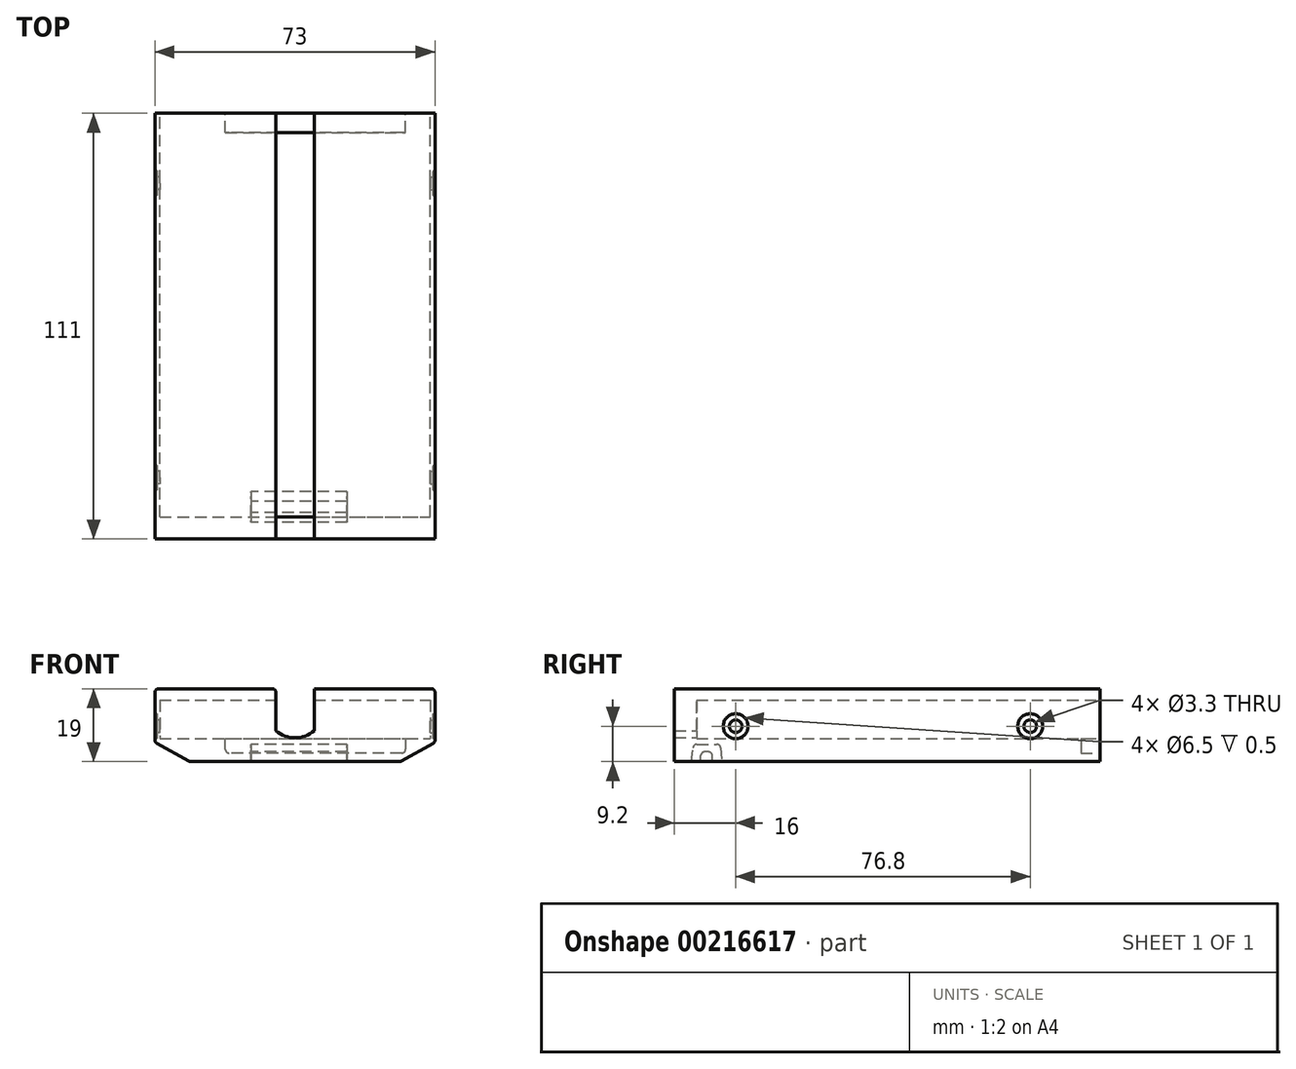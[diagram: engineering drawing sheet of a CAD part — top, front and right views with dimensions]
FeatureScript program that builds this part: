
annotation { "Feature Type Name" : "Feature", "Feature Type Description" : "" }
export const myFeature = defineFeature(function(context is Context, id is Id, definition is map)
    precondition{}
    {
        {
            var Q0;
            Q0=qCreatedBy(makeId("Front.planeOp"),FACE);
            var sketch = newSketch(context, id + "F0", { "sketchPlane" : qUnion([Q0])});
            skLineSegment(sketch, "E0", {"start": v(0, 19) * mm, "end": v(73, 19) * mm});
            skLineSegment(sketch, "E1", {"start": v(73, 19) * mm, "end": v(73, 5) * mm});
            skLineSegment(sketch, "E2", {"start": v(73, 5) * mm, "end": v(64, 0) * mm});
            skLineSegment(sketch, "E3", {"start": v(64, 0) * mm, "end": v(9, 0) * mm});
            skLineSegment(sketch, "E4", {"start": v(9, 0) * mm, "end": v(0, 5) * mm});
            skLineSegment(sketch, "E5", {"start": v(0, 5) * mm, "end": v(0, 19) * mm});
            skSolve(sketch);
        }
        {
            var Q0;
            Q0 = qSketchRegion(id + "F0", true);
            extrude(context, id + "F1", {"entities" : qUnion([Q0]), "depth" : 111 * mm});
        }
        {
            var Q0;
            Q0=qCreatedBy(makeId("Front.planeOp"),FACE);
            var sketch = newSketch(context, id + "F2", { "sketchPlane" : qUnion([Q0])});
            skLineSegment(sketch, "E6.bottom", {"start": v(1.25, 16) * mm, "end": v(71.75, 16) * mm});
            skLineSegment(sketch, "E6.top", {"start": v(1.25, 6) * mm, "end": v(71.75, 6) * mm});
            skLineSegment(sketch, "E6.left", {"start": v(1.25, 16) * mm, "end": v(1.25, 6) * mm});
            skLineSegment(sketch, "E6.right", {"start": v(71.75, 16) * mm, "end": v(71.75, 6) * mm});
            skSolve(sketch);
        }
        {
            var Q0;
            Q0 = qSketchRegion(id + "F2", true);
            extrude(context, id + "F3", {"entities" : qUnion([Q0]), "operationType" : NewBodyOperationType.REMOVE, "depth" : 105.2 * mm});
        }
        {
            var Q0;
            Q0=qCreatedBy(makeId("Front.planeOp"),FACE);
            var sketch = newSketch(context, id + "F4", { "sketchPlane" : qUnion([Q0])});
            skLineSegment(sketch, "E7", {"start": v(31.5, 19) * mm, "end": v(41.5, 19) * mm});
            skLineSegment(sketch, "E8", {"start": v(41.5, 19) * mm, "end": v(41.5, 8) * mm});
            skLineSegment(sketch, "E9", {"start": v(31.5, 19) * mm, "end": v(31.5, 8) * mm});
            skArc(sketch, "E10", {"start": v(31.5, 8) * mm, "mid": v(36.5, 6.19) * mm, "end": v(41.5, 8) * mm});
            skSolve(sketch);
        }
        {
            var Q0;
            Q0 = qSketchRegion(id + "F4", true);
            extrude(context, id + "F5", {"entities" : qUnion([Q0]), "operationType" : NewBodyOperationType.REMOVE, "depth" : 150 * mm});
        }
        {
            var Q0;
            Q0=qCreatedBy(makeId("Right.planeOp"),FACE);
            var sketch = newSketch(context, id + "F6", { "sketchPlane" : qUnion([Q0])});
            skPoint(sketch, "E11", {"position": v(-18.2, 9.2) * mm});
            skPoint(sketch, "E12", {"position": v(-95, 9.2) * mm});
            skSolve(sketch);
        }
        {
            var Q0;
            Q0=sQuery(id+"F6.wireOp",VERTEX,"E12");
            var Q1;
            Q1=sQuery(id+"F6.wireOp",VERTEX,"E11");
            var Q2;
            Q2=makeQuery(id+"F1.opExtrude","SWEPT_BODY",BODY,{"disambiguationData":[OSD([sQuery(id+"F0.wireOp",EDGE,"E0"),sQuery(id+"F0.wireOp",EDGE,"E1"),sQuery(id+"F0.wireOp",EDGE,"E2"),sQuery(id+"F0.wireOp",EDGE,"E3"),sQuery(id+"F0.wireOp",EDGE,"E4"),sQuery(id+"F0.wireOp",EDGE,"E5")])]});
            hole(context, id + "F7", {"style" : HoleStyle.C_BORE, "endStyle" : HoleEndStyle.BLIND, "oppositeDirection" : true, "holeDiameter" : 3.3 * mm, "cBoreDiameter" : 6.5 * mm, "cBoreDepth" : 0.5 * mm, "holeDepth" : 5 * mm, "startFromSketch" : true, "locations" : qUnion([Q0, Q1]), "scope" : qUnion([Q2])});
        }
        {
            var Q0;
            Q0=makeQuery(id+"F1.opExtrude","SWEPT_FACE",FACE,{"disambiguationData":[OSD([sQuery(id+"F0.wireOp",EDGE,"E1")])]});
            var sketch = newSketch(context, id + "F8", { "sketchPlane" : qUnion([Q0])});
            skPoint(sketch, "E13", {"position": v(-95, 9.2) * mm});
            skPoint(sketch, "E14", {"position": v(-18.2, 9.2) * mm});
            skSolve(sketch);
        }
        {
            var Q0;
            Q0=sQuery(id+"F8.wireOp",VERTEX,"E13");
            var Q1;
            Q1=sQuery(id+"F8.wireOp",VERTEX,"E14");
            var Q2;
            Q2=makeQuery(id+"F1.opExtrude","SWEPT_BODY",BODY,{"disambiguationData":[OSD([sQuery(id+"F0.wireOp",EDGE,"E0"),sQuery(id+"F0.wireOp",EDGE,"E1"),sQuery(id+"F0.wireOp",EDGE,"E2"),sQuery(id+"F0.wireOp",EDGE,"E3"),sQuery(id+"F0.wireOp",EDGE,"E4"),sQuery(id+"F0.wireOp",EDGE,"E5")])]});
            hole(context, id + "F9", {"style" : HoleStyle.C_BORE, "endStyle" : HoleEndStyle.BLIND, "holeDiameter" : 3.3 * mm, "cBoreDiameter" : 6.5 * mm, "cBoreDepth" : 0.5 * mm, "holeDepth" : 5 * mm, "startFromSketch" : true, "locations" : qUnion([Q0, Q1]), "scope" : qUnion([Q2])});
        }
        {
            var Q0;
            Q0=qCreatedBy(makeId("Right.planeOp"),FACE);
            var sketch = newSketch(context, id + "F10", { "sketchPlane" : qUnion([Q0])});
            skLineSegment(sketch, "E15", {"start": v(-105.13, 4.5) * mm, "end": v(-99.92, 4.5) * mm});
            skLineSegment(sketch, "E16", {"start": v(-101.1, 0) * mm, "end": v(-101.1, 1.5) * mm});
            skLineSegment(sketch, "E17", {"start": v(-102.1, 2.5) * mm, "end": v(-103.1, 2.5) * mm});
            skLineSegment(sketch, "E18", {"start": v(-104.1, 0) * mm, "end": v(-104.1, 1.5) * mm});
            skPoint(sketch, "E19.visualSharp", {"position": v(-101.1, 2.5) * mm});
            skArc(sketch, "E19.filletArc", {"start": v(-101.1, 1.5) * mm, "mid": v(-101.4, 2.2) * mm, "end": v(-102.1, 2.5) * mm});
            skPoint(sketch, "E20.visualSharp", {"position": v(-104.1, 2.5) * mm});
            skArc(sketch, "E20.filletArc", {"start": v(-103.1, 2.5) * mm, "mid": v(-103.81, 2.2) * mm, "end": v(-104.1, 1.5) * mm});
            skLineSegment(sketch, "E21", {"start": v(-98.92, 3.59) * mm, "end": v(-98.6, 0) * mm});
            skLineSegment(sketch, "E22", {"start": v(-98.6, 0) * mm, "end": v(-101.1, 0) * mm});
            skLineSegment(sketch, "E23", {"start": v(-104.1, 0) * mm, "end": v(-106.6, 0) * mm});
            skLineSegment(sketch, "E24", {"start": v(-106.6, 0) * mm, "end": v(-106.12, 3.63) * mm});
            skPoint(sketch, "E25.visualSharp", {"position": v(-99, 4.5) * mm});
            skArc(sketch, "E25.filletArc", {"start": v(-98.92, 3.59) * mm, "mid": v(-99.24, 4.24) * mm, "end": v(-99.92, 4.5) * mm});
            skPoint(sketch, "E26.visualSharp", {"position": v(-106, 4.5) * mm});
            skArc(sketch, "E26.filletArc", {"start": v(-105.13, 4.5) * mm, "mid": v(-105.78, 4.25) * mm, "end": v(-106.12, 3.63) * mm});
            skSolve(sketch);
        }
        {
            var Q0;
            Q0 = qSketchRegion(id + "F10", true);
            extrude(context, id + "F11", {"entities" : qUnion([Q0]), "operationType" : NewBodyOperationType.REMOVE, "depth" : 50 * mm, "hasSecondDirection" : true, "secondDirectionOppositeDirection" : false, "secondDirectionDepth" : 25 * mm});
        }
        {
            var Q0;
            Q0=makeQuery(id+"F1.opExtrude","SWEPT_EDGE",EDGE,{"disambiguationData":[OSD([sQuery(id+"F0.wireOp",EDGE,"E0"),sQuery(id+"F0.wireOp",EDGE,"E1")])]});
            var Q1;
            Q1=makeQuery(id+"F1.opExtrude","SWEPT_EDGE",EDGE,{"disambiguationData":[OSD([sQuery(id+"F0.wireOp",EDGE,"E0"),sQuery(id+"F0.wireOp",EDGE,"E5")])]});
            var Q2;
            Q2=makeQuery(id+"F5.boolean.opBoolean","COPY",EDGE,{"derivedFrom":makeQuery(id+"F5.opExtrude","SWEPT_EDGE",EDGE,{"disambiguationData":[OSD([sQuery(id+"F4.wireOp",EDGE,"E7"),sQuery(id+"F4.wireOp",EDGE,"E9")])]})});
            var Q3;
            Q3=makeQuery(id+"F5.boolean.opBoolean","COPY",EDGE,{"derivedFrom":makeQuery(id+"F5.opExtrude","SWEPT_EDGE",EDGE,{"disambiguationData":[OSD([sQuery(id+"F4.wireOp",EDGE,"E7"),sQuery(id+"F4.wireOp",EDGE,"E8")])]})});
            var Q4;
            Q4=makeQuery(id+"F1.opExtrude","SWEPT_EDGE",EDGE,{"disambiguationData":[OSD([sQuery(id+"F0.wireOp",EDGE,"E3"),sQuery(id+"F0.wireOp",EDGE,"E4")])]});
            var Q5;
            Q5=makeQuery(id+"F1.opExtrude","SWEPT_EDGE",EDGE,{"disambiguationData":[OSD([sQuery(id+"F0.wireOp",EDGE,"E2"),sQuery(id+"F0.wireOp",EDGE,"E3")])]});
            var Q6;
            Q6=makeQuery(id+"F1.opExtrude","SWEPT_EDGE",EDGE,{"disambiguationData":[OSD([sQuery(id+"F0.wireOp",EDGE,"E1"),sQuery(id+"F0.wireOp",EDGE,"E2")])]});
            var Q7;
            Q7=makeQuery(id+"F1.opExtrude","SWEPT_EDGE",EDGE,{"disambiguationData":[OSD([sQuery(id+"F0.wireOp",EDGE,"E4"),sQuery(id+"F0.wireOp",EDGE,"E5")])]});
            fillet(context, id + "F12", {"entities" : qUnion([Q0, Q1, Q2, Q3, Q4, Q5, Q6, Q7]), "radius" : 1 * mm, "tangentPropagation" : true, "allowEdgeOverflow" : false});
        }
        {
            var Q0;
            Q0=makeQuery(id+"F1.opExtrude","CAP_FACE",FACE,{"disambiguationData":[OSD([sQuery(id+"F0.wireOp",EDGE,"E0"),sQuery(id+"F0.wireOp",EDGE,"E1"),sQuery(id+"F0.wireOp",EDGE,"E2"),sQuery(id+"F0.wireOp",EDGE,"E3"),sQuery(id+"F0.wireOp",EDGE,"E4"),sQuery(id+"F0.wireOp",EDGE,"E5")])],"isStart":true});
            var sketch = newSketch(context, id + "F13", { "sketchPlane" : qUnion([Q0])});
            skLineSegment(sketch, "E27", {"start": v(-65.35, 6) * mm, "end": v(-65.35, 3.2) * mm});
            skLineSegment(sketch, "E28", {"start": v(-64.35, 2.2) * mm, "end": v(-19.35, 2.2) * mm});
            skLineSegment(sketch, "E29", {"start": v(-18.35, 3.2) * mm, "end": v(-18.35, 6) * mm});
            skPoint(sketch, "E30.visualSharp", {"position": v(-65.35, 2.2) * mm});
            skArc(sketch, "E30.filletArc", {"start": v(-65.35, 3.2) * mm, "mid": v(-65.06, 2.5) * mm, "end": v(-64.35, 2.2) * mm});
            skPoint(sketch, "E31.visualSharp", {"position": v(-18.35, 2.2) * mm});
            skArc(sketch, "E31.filletArc", {"start": v(-19.35, 2.2) * mm, "mid": v(-18.64, 2.5) * mm, "end": v(-18.35, 3.2) * mm});
            skSolve(sketch);
        }
        {
            var Q0;
            {var subQ1=sQuery(id+"F13.wireOp",EDGE,"E27");Q0=makeQuery(id+"F13.imprint","IMPRINT",FACE,{"disambiguationData":[TD([[makeQuery(id+"F13.imprint","IMPRINT",EDGE,{"derivedFrom":subQ1}),1.0]])]});}
            extrude(context, id + "F14", {"entities" : qUnion([Q0]), "operationType" : NewBodyOperationType.REMOVE, "oppositeDirection" : true, "depth" : 5 * mm});
        }
    });
